SOLIDWORKS PART (.sldprt)
format: sldprt  version: not decoded by parser v0  size: 126,464 bytes
history: native  units: mm
features: sketch x4, extrude x4, plane x3, material x1, fillet x1 (+9 scaffold rows collapsed)
feature tree (22):
  scaffold x9  (default folders/planes/origin — collapsed)
  material  "Matériau <non spécifié>"
  plane  "Face"
  plane  "Dessus"
  plane  "Droite"
  sketch  "Esquisse1"
  extrude  "Base-Extrusion"  Depth=0.9mm
  sketch  "Esquisse2"  dims[D1=0.15mm D2=0.15mm]
  extrude  "Boss.-Extru.1"  Depth=0.5mm
  sketch  "Esquisse3"
  extrude  "Boss.-Extru.2"  Depth=6mm
  sketch  "Esquisse4"  dims[D1=~4.348335mm]
  extrude  "Boss.-Extru.3"  Depth=0.2mm
  fillet  "Congé1"  Radius=0.45mm
decode coverage: 7 of 9 modeling features carry decoded parameters
note: ~ marks probable driven/reference dimensions
note: suppression state not decoded; provenance and decode notes live in map.json
